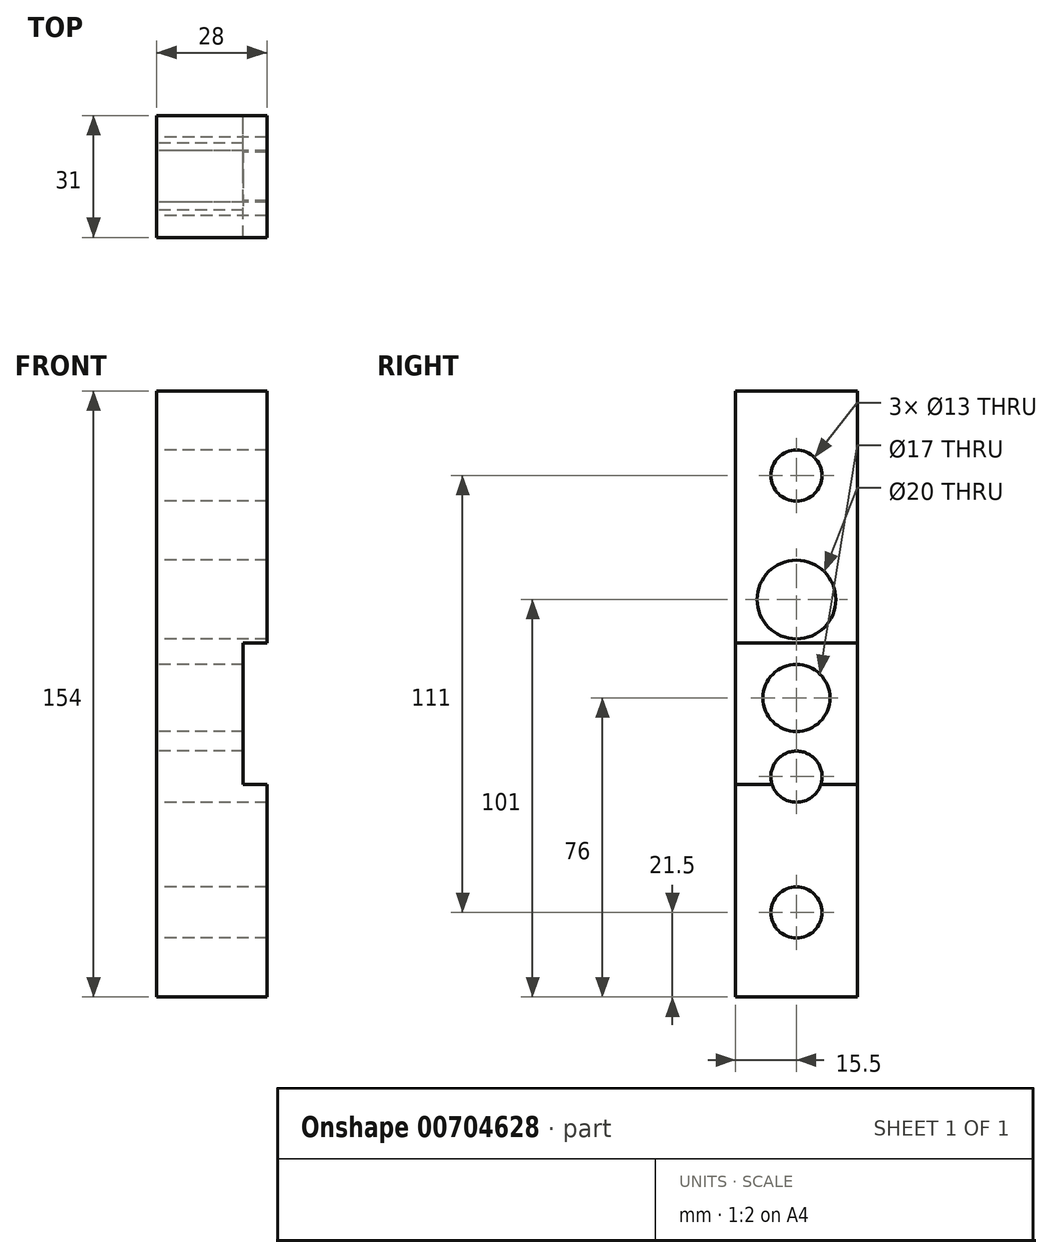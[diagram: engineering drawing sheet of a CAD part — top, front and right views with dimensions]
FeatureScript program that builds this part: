
annotation { "Feature Type Name" : "Feature", "Feature Type Description" : "" }
export const myFeature = defineFeature(function(context is Context, id is Id, definition is map)
    precondition{}
    {
        {
            var Q0;
            Q0=qCreatedBy(makeId("Front.planeOp"),FACE);
            var sketch = newSketch(context, id + "F0", { "sketchPlane" : qUnion([Q0])});
            skLineSegment(sketch, "E0.bottom", {"start": v(14, 77) * mm, "end": v(-14, 77) * mm});
            skLineSegment(sketch, "E0.top", {"start": v(14, -77) * mm, "end": v(-14, -77) * mm});
            skLineSegment(sketch, "E0.left", {"start": v(14, 77) * mm, "end": v(14, -77) * mm});
            skLineSegment(sketch, "E0.right", {"start": v(-14, 77) * mm, "end": v(-14, -77) * mm});
            skPoint(sketch, "E0.middle", {"position": v(0, 0) * mm});
            skLineSegment(sketch, "E1.bottom", {"start": v(14, 13) * mm, "end": v(8, 13) * mm});
            skLineSegment(sketch, "E1.top", {"start": v(14, -23) * mm, "end": v(8, -23) * mm});
            skLineSegment(sketch, "E1.left", {"start": v(14, 13) * mm, "end": v(14, -23) * mm});
            skLineSegment(sketch, "E1.right", {"start": v(8, 13) * mm, "end": v(8, -23) * mm});
            skSolve(sketch);
        }
        {
            var Q0;
            {var subQ4=sQuery(id+"F0.wireOp",EDGE,"E0.bottom");Q0=makeQuery(id+"F0.imprint","IMPRINT",FACE,{"disambiguationData":[TD([[makeQuery(id+"F0.imprint","IMPRINT",EDGE,{"derivedFrom":subQ4}),1.0]])]});}
            extrude(context, id + "F1", {"entities" : qUnion([Q0]), "endBound" : BoundingType.SYMMETRIC, "depth" : 31 * mm, "offsetDistance" : 25 * mm});
        }
        {
            var Q0;
            Q0=makeQuery(id+"F1.opExtrude","SWEPT_FACE",FACE,{"disambiguationData":[OSD([sQuery(id+"F0.wireOp",EDGE,"E0.right")])]});
            var sketch = newSketch(context, id + "F2", { "sketchPlane" : qUnion([Q0])});
            skCircle(sketch, "E2", {"center": v(0, -55.5) * mm, "radius": 6.5 * mm});
            skCircle(sketch, "E3", {"center": v(0, -21) * mm, "radius": 6.5 * mm});
            skCircle(sketch, "E4", {"center": v(0, -1) * mm, "radius": 8.5 * mm});
            skCircle(sketch, "E5", {"center": v(0, 24) * mm, "radius": 10 * mm});
            skCircle(sketch, "E6", {"center": v(0, 55.5) * mm, "radius": 6.5 * mm});
            skSolve(sketch);
        }
        {
            var Q0;
            Q0=makeQuery(id+"F2.imprint","IMPRINT",FACE,{"disambiguationData":[TD([[makeQuery(id+"F2.imprint","IMPRINT",EDGE,{"derivedFrom":sQuery(id+"F2.wireOp",EDGE,"E6")}),1.0]])]});
            var Q1;
            Q1=makeQuery(id+"F2.imprint","IMPRINT",FACE,{"disambiguationData":[TD([[makeQuery(id+"F2.imprint","IMPRINT",EDGE,{"derivedFrom":sQuery(id+"F2.wireOp",EDGE,"E5")}),1.0]])]});
            var Q2;
            Q2=makeQuery(id+"F2.imprint","IMPRINT",FACE,{"disambiguationData":[TD([[makeQuery(id+"F2.imprint","IMPRINT",EDGE,{"derivedFrom":sQuery(id+"F2.wireOp",EDGE,"E4")}),1.0]])]});
            var Q3;
            Q3=makeQuery(id+"F2.imprint","IMPRINT",FACE,{"disambiguationData":[TD([[makeQuery(id+"F2.imprint","IMPRINT",EDGE,{"derivedFrom":sQuery(id+"F2.wireOp",EDGE,"E3")}),1.0]])]});
            var Q4;
            Q4=makeQuery(id+"F2.imprint","IMPRINT",FACE,{"disambiguationData":[TD([[makeQuery(id+"F2.imprint","IMPRINT",EDGE,{"derivedFrom":sQuery(id+"F2.wireOp",EDGE,"E2")}),1.0]])]});
            extrude(context, id + "F3", {"entities" : qUnion([Q0, Q1, Q2, Q3, Q4]), "operationType" : NewBodyOperationType.REMOVE, "endBound" : BoundingType.THROUGH_ALL, "oppositeDirection" : true, "depth" : 25 * mm, "offsetDistance" : 25 * mm});
        }
    });
